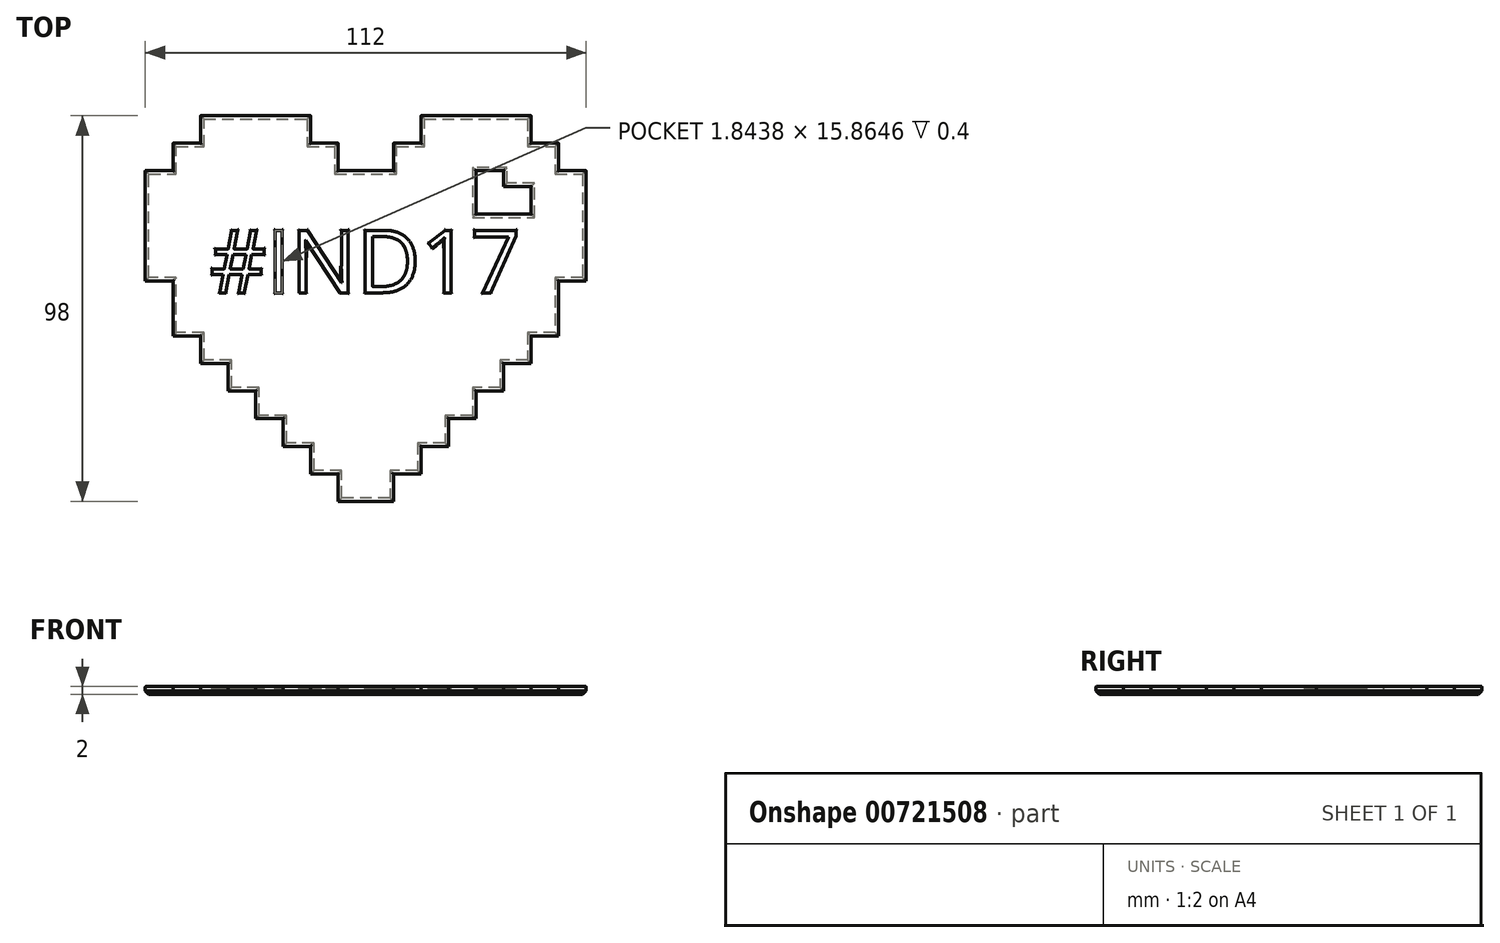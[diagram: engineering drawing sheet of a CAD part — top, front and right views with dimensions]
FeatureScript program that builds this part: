
annotation { "Feature Type Name" : "Feature", "Feature Type Description" : "" }
export const myFeature = defineFeature(function(context is Context, id is Id, definition is map)
    precondition{}
    {
        {
            assignVariable(context, id + "F0", {"variableType" : VariableType.NUMBER, "name" : "scale", "numberValue" : 7});
        }
        {
            var Q0;
            Q0=qCreatedBy(makeId("Top.planeOp"),FACE);
            var sketch = newSketch(context, id + "F1", { "sketchPlane" : qUnion([Q0])});
            skLineSegment(sketch, "E0", {"start": v(25.3, 16.05) * mm, "end": v(25.3, 20.05) * mm});
            skLineSegment(sketch, "E1", {"start": v(18.3, 20.05) * mm, "end": v(18.3, 9.05) * mm});
            skLineSegment(sketch, "E2", {"start": v(18.3, 9.05) * mm, "end": v(32.3, 9.05) * mm});
            skLineSegment(sketch, "E3", {"start": v(32.3, 9.05) * mm, "end": v(32.3, 16.05) * mm});
            skLineSegment(sketch, "E4", {"start": v(32.3, 16.05) * mm, "end": v(25.3, 16.05) * mm});
            skLineSegment(sketch, "E5", {"start": v(39.3, 20.05) * mm, "end": v(39.3, 27.05) * mm});
            skLineSegment(sketch, "E6", {"start": v(39.3, 27.05) * mm, "end": v(32.3, 27.05) * mm});
            skLineSegment(sketch, "E7", {"start": v(32.3, 27.05) * mm, "end": v(32.3, 34.05) * mm});
            skLineSegment(sketch, "E8", {"start": v(32.3, 34.05) * mm, "end": v(4.3, 34.05) * mm});
            skLineSegment(sketch, "E9", {"start": v(4.3, 34.05) * mm, "end": v(4.3, 27.05) * mm});
            skLineSegment(sketch, "E10", {"start": v(4.3, 27.05) * mm, "end": v(-2.7, 27.05) * mm});
            skLineSegment(sketch, "E11", {"start": v(-2.7, 27.05) * mm, "end": v(-2.7, 20.05) * mm});
            skLineSegment(sketch, "E12", {"start": v(-2.7, 20.05) * mm, "end": v(-16.7, 20.05) * mm});
            skLineSegment(sketch, "E13", {"start": v(-16.7, 20.05) * mm, "end": v(-16.7, 27.05) * mm});
            skLineSegment(sketch, "E14", {"start": v(-16.7, 27.05) * mm, "end": v(-23.7, 27.05) * mm});
            skLineSegment(sketch, "E15", {"start": v(-23.7, 27.05) * mm, "end": v(-23.7, 34.05) * mm});
            skLineSegment(sketch, "E16", {"start": v(-23.7, 34.05) * mm, "end": v(-51.7, 34.05) * mm});
            skLineSegment(sketch, "E17", {"start": v(-51.7, 34.05) * mm, "end": v(-51.7, 27.05) * mm});
            skLineSegment(sketch, "E18", {"start": v(-51.7, 27.05) * mm, "end": v(-58.7, 27.05) * mm});
            skLineSegment(sketch, "E19", {"start": v(-58.7, 27.05) * mm, "end": v(-58.7, 20.05) * mm});
            skLineSegment(sketch, "E20", {"start": v(-58.7, 20.05) * mm, "end": v(-65.7, 20.05) * mm});
            skLineSegment(sketch, "E21", {"start": v(-65.7, 20.05) * mm, "end": v(-65.7, -7.95) * mm});
            skLineSegment(sketch, "E22", {"start": v(-65.7, -7.95) * mm, "end": v(-58.7, -7.95) * mm});
            skLineSegment(sketch, "E23", {"start": v(-58.7, -7.95) * mm, "end": v(-58.7, -21.95) * mm});
            skLineSegment(sketch, "E24", {"start": v(-58.7, -21.95) * mm, "end": v(-51.7, -21.95) * mm});
            skLineSegment(sketch, "E25", {"start": v(-51.7, -21.95) * mm, "end": v(-51.7, -28.95) * mm});
            skLineSegment(sketch, "E26", {"start": v(-51.7, -28.95) * mm, "end": v(-44.7, -28.95) * mm});
            skLineSegment(sketch, "E27", {"start": v(-44.7, -28.95) * mm, "end": v(-44.7, -35.95) * mm});
            skLineSegment(sketch, "E28", {"start": v(-44.7, -35.95) * mm, "end": v(-37.7, -35.95) * mm});
            skLineSegment(sketch, "E29", {"start": v(-37.7, -35.95) * mm, "end": v(-37.7, -42.95) * mm});
            skLineSegment(sketch, "E30", {"start": v(-37.7, -42.95) * mm, "end": v(-30.7, -42.95) * mm});
            skLineSegment(sketch, "E31", {"start": v(-30.7, -42.95) * mm, "end": v(-30.7, -49.95) * mm});
            skLineSegment(sketch, "E32", {"start": v(-30.7, -49.95) * mm, "end": v(-23.7, -49.95) * mm});
            skLineSegment(sketch, "E33", {"start": v(-23.7, -49.95) * mm, "end": v(-23.7, -56.95) * mm});
            skLineSegment(sketch, "E34", {"start": v(-23.7, -56.95) * mm, "end": v(-16.7, -56.95) * mm});
            skLineSegment(sketch, "E35", {"start": v(-16.7, -56.95) * mm, "end": v(-16.7, -63.95) * mm});
            skLineSegment(sketch, "E36", {"start": v(-16.7, -63.95) * mm, "end": v(-2.7, -63.95) * mm});
            skLineSegment(sketch, "E37", {"start": v(-2.7, -63.95) * mm, "end": v(-2.7, -56.95) * mm});
            skLineSegment(sketch, "E38", {"start": v(-2.7, -56.95) * mm, "end": v(4.3, -56.95) * mm});
            skLineSegment(sketch, "E39", {"start": v(4.3, -56.95) * mm, "end": v(4.3, -49.95) * mm});
            skLineSegment(sketch, "E40", {"start": v(4.3, -49.95) * mm, "end": v(11.3, -49.95) * mm});
            skLineSegment(sketch, "E41", {"start": v(11.3, -49.95) * mm, "end": v(11.3, -42.95) * mm});
            skLineSegment(sketch, "E42", {"start": v(11.3, -42.95) * mm, "end": v(18.3, -42.95) * mm});
            skLineSegment(sketch, "E43", {"start": v(18.3, -42.95) * mm, "end": v(18.3, -35.95) * mm});
            skLineSegment(sketch, "E44", {"start": v(18.3, -35.95) * mm, "end": v(25.3, -35.95) * mm});
            skLineSegment(sketch, "E45", {"start": v(25.3, -35.95) * mm, "end": v(25.3, -28.95) * mm});
            skLineSegment(sketch, "E46", {"start": v(25.3, -28.95) * mm, "end": v(32.3, -28.95) * mm});
            skLineSegment(sketch, "E47", {"start": v(32.3, -28.95) * mm, "end": v(32.3, -21.95) * mm});
            skLineSegment(sketch, "E48", {"start": v(32.3, -21.95) * mm, "end": v(39.3, -21.95) * mm});
            skLineSegment(sketch, "E49", {"start": v(39.3, -21.95) * mm, "end": v(39.3, -7.95) * mm});
            skLineSegment(sketch, "E50", {"start": v(39.3, -7.95) * mm, "end": v(46.3, -7.95) * mm});
            skLineSegment(sketch, "E51", {"start": v(46.3, -7.95) * mm, "end": v(46.3, 20.05) * mm});
            skLineSegment(sketch, "E52", {"start": v(46.3, 20.05) * mm, "end": v(39.3, 20.05) * mm});
            skLineSegment(sketch, "E53", {"start": v(18.3, 20.05) * mm, "end": v(25.3, 20.05) * mm});
            skSolve(sketch);
        }
        {
            var Q0;
            Q0=makeQuery(id+"F1.imprint","IMPRINT",FACE,{"disambiguationData":[TD([[makeQuery(id+"F1.imprint","IMPRINT",EDGE,{"derivedFrom":sQuery(id+"F1.wireOp",EDGE,"E0")}),-1.0]])]});
            extrude(context, id + "F2", {"entities" : qUnion([Q0]), "depth" : 2 * mm, "offsetDistance" : 25 * mm});
        }
        {
            var Q0;
            Q0=makeQuery(id+"F2.opExtrude","CAP_FACE",FACE,{"disambiguationData":[OSD([sQuery(id+"F1.wireOp",EDGE,"E0"),sQuery(id+"F1.wireOp",EDGE,"E1"),sQuery(id+"F1.wireOp",EDGE,"E2"),sQuery(id+"F1.wireOp",EDGE,"E3"),sQuery(id+"F1.wireOp",EDGE,"E4"),sQuery(id+"F1.wireOp",EDGE,"E5"),sQuery(id+"F1.wireOp",EDGE,"E6"),sQuery(id+"F1.wireOp",EDGE,"E7"),sQuery(id+"F1.wireOp",EDGE,"E8"),sQuery(id+"F1.wireOp",EDGE,"E9"),sQuery(id+"F1.wireOp",EDGE,"E10"),sQuery(id+"F1.wireOp",EDGE,"E11"),sQuery(id+"F1.wireOp",EDGE,"E12"),sQuery(id+"F1.wireOp",EDGE,"E13"),sQuery(id+"F1.wireOp",EDGE,"E14"),sQuery(id+"F1.wireOp",EDGE,"E15"),sQuery(id+"F1.wireOp",EDGE,"E16"),sQuery(id+"F1.wireOp",EDGE,"E17"),sQuery(id+"F1.wireOp",EDGE,"E18"),sQuery(id+"F1.wireOp",EDGE,"E19"),sQuery(id+"F1.wireOp",EDGE,"E20"),sQuery(id+"F1.wireOp",EDGE,"E21"),sQuery(id+"F1.wireOp",EDGE,"E22"),sQuery(id+"F1.wireOp",EDGE,"E23"),sQuery(id+"F1.wireOp",EDGE,"E24"),sQuery(id+"F1.wireOp",EDGE,"E25"),sQuery(id+"F1.wireOp",EDGE,"E26"),sQuery(id+"F1.wireOp",EDGE,"E27"),sQuery(id+"F1.wireOp",EDGE,"E28"),sQuery(id+"F1.wireOp",EDGE,"E29"),sQuery(id+"F1.wireOp",EDGE,"E30"),sQuery(id+"F1.wireOp",EDGE,"E31"),sQuery(id+"F1.wireOp",EDGE,"E32"),sQuery(id+"F1.wireOp",EDGE,"E33"),sQuery(id+"F1.wireOp",EDGE,"E34"),sQuery(id+"F1.wireOp",EDGE,"E35"),sQuery(id+"F1.wireOp",EDGE,"E36"),sQuery(id+"F1.wireOp",EDGE,"E37"),sQuery(id+"F1.wireOp",EDGE,"E38"),sQuery(id+"F1.wireOp",EDGE,"E39"),sQuery(id+"F1.wireOp",EDGE,"E40"),sQuery(id+"F1.wireOp",EDGE,"E41"),sQuery(id+"F1.wireOp",EDGE,"E42"),sQuery(id+"F1.wireOp",EDGE,"E43"),sQuery(id+"F1.wireOp",EDGE,"E44"),sQuery(id+"F1.wireOp",EDGE,"E45"),sQuery(id+"F1.wireOp",EDGE,"E46"),sQuery(id+"F1.wireOp",EDGE,"E47"),sQuery(id+"F1.wireOp",EDGE,"E48"),sQuery(id+"F1.wireOp",EDGE,"E49"),sQuery(id+"F1.wireOp",EDGE,"E50"),sQuery(id+"F1.wireOp",EDGE,"E51"),sQuery(id+"F1.wireOp",EDGE,"E52"),sQuery(id+"F1.wireOp",EDGE,"E53")])],"isStart":true});
            chamfer(context, id + "F3", {"entities" : qUnion([Q0]), "width" : (getVariable(context, 'scale') / 8) * mm, "tangentPropagation" : true});
        }
        {
            var Q0;
            Q0=makeQuery(id+"F2.opExtrude","CAP_FACE",FACE,{"disambiguationData":[OSD([sQuery(id+"F1.wireOp",EDGE,"E0"),sQuery(id+"F1.wireOp",EDGE,"E1"),sQuery(id+"F1.wireOp",EDGE,"E2"),sQuery(id+"F1.wireOp",EDGE,"E3"),sQuery(id+"F1.wireOp",EDGE,"E4"),sQuery(id+"F1.wireOp",EDGE,"E5"),sQuery(id+"F1.wireOp",EDGE,"E6"),sQuery(id+"F1.wireOp",EDGE,"E7"),sQuery(id+"F1.wireOp",EDGE,"E8"),sQuery(id+"F1.wireOp",EDGE,"E9"),sQuery(id+"F1.wireOp",EDGE,"E10"),sQuery(id+"F1.wireOp",EDGE,"E11"),sQuery(id+"F1.wireOp",EDGE,"E12"),sQuery(id+"F1.wireOp",EDGE,"E13"),sQuery(id+"F1.wireOp",EDGE,"E14"),sQuery(id+"F1.wireOp",EDGE,"E15"),sQuery(id+"F1.wireOp",EDGE,"E16"),sQuery(id+"F1.wireOp",EDGE,"E17"),sQuery(id+"F1.wireOp",EDGE,"E18"),sQuery(id+"F1.wireOp",EDGE,"E19"),sQuery(id+"F1.wireOp",EDGE,"E20"),sQuery(id+"F1.wireOp",EDGE,"E21"),sQuery(id+"F1.wireOp",EDGE,"E22"),sQuery(id+"F1.wireOp",EDGE,"E23"),sQuery(id+"F1.wireOp",EDGE,"E24"),sQuery(id+"F1.wireOp",EDGE,"E25"),sQuery(id+"F1.wireOp",EDGE,"E26"),sQuery(id+"F1.wireOp",EDGE,"E27"),sQuery(id+"F1.wireOp",EDGE,"E28"),sQuery(id+"F1.wireOp",EDGE,"E29"),sQuery(id+"F1.wireOp",EDGE,"E30"),sQuery(id+"F1.wireOp",EDGE,"E31"),sQuery(id+"F1.wireOp",EDGE,"E32"),sQuery(id+"F1.wireOp",EDGE,"E33"),sQuery(id+"F1.wireOp",EDGE,"E34"),sQuery(id+"F1.wireOp",EDGE,"E35"),sQuery(id+"F1.wireOp",EDGE,"E36"),sQuery(id+"F1.wireOp",EDGE,"E37"),sQuery(id+"F1.wireOp",EDGE,"E38"),sQuery(id+"F1.wireOp",EDGE,"E39"),sQuery(id+"F1.wireOp",EDGE,"E40"),sQuery(id+"F1.wireOp",EDGE,"E41"),sQuery(id+"F1.wireOp",EDGE,"E42"),sQuery(id+"F1.wireOp",EDGE,"E43"),sQuery(id+"F1.wireOp",EDGE,"E44"),sQuery(id+"F1.wireOp",EDGE,"E45"),sQuery(id+"F1.wireOp",EDGE,"E46"),sQuery(id+"F1.wireOp",EDGE,"E47"),sQuery(id+"F1.wireOp",EDGE,"E48"),sQuery(id+"F1.wireOp",EDGE,"E49"),sQuery(id+"F1.wireOp",EDGE,"E50"),sQuery(id+"F1.wireOp",EDGE,"E51"),sQuery(id+"F1.wireOp",EDGE,"E52"),sQuery(id+"F1.wireOp",EDGE,"E53")])],"isStart":false});
            var sketch = newSketch(context, id + "F4", { "sketchPlane" : qUnion([Q0])});
            skText(sketch, "E54", { "text": "#IND17", "fontName": "OpenSans-Regular.ttf"});
            skLineSegment(sketch, "E55", {"start": v(-9.7, 20.05) * mm, "end": v(-9.7, -63.95) * mm, "construction": true});
            const initialGuessF4  = {"E54": [-0.04931, -0.01095, 1, 0, 0.016]};
            skSetInitialGuess(sketch, initialGuessF4);
            skSolve(sketch);
        }
        {
            var Q0;
            Q0 = qSketchRegion(id + "F4", true);
            extrude(context, id + "F5", {"entities" : qUnion([Q0]), "operationType" : NewBodyOperationType.REMOVE, "oppositeDirection" : true, "depth" : 0.6 * mm, "offsetDistance" : 25 * mm});
        }
        {
            var Q0;
            {var subQ0=sQuery(id+"F1.wireOp",EDGE,"E53");var subQ1=sQuery(id+"F1.wireOp",EDGE,"E52");var subQ2=sQuery(id+"F1.wireOp",EDGE,"E51");var subQ3=sQuery(id+"F1.wireOp",EDGE,"E50");var subQ4=sQuery(id+"F1.wireOp",EDGE,"E49");var subQ5=sQuery(id+"F1.wireOp",EDGE,"E48");var subQ6=sQuery(id+"F1.wireOp",EDGE,"E47");var subQ7=sQuery(id+"F1.wireOp",EDGE,"E46");var subQ8=sQuery(id+"F1.wireOp",EDGE,"E20");var subQ9=sQuery(id+"F1.wireOp",EDGE,"E19");var subQ10=sQuery(id+"F1.wireOp",EDGE,"E18");var subQ11=sQuery(id+"F1.wireOp",EDGE,"E17");var subQ12=sQuery(id+"F1.wireOp",EDGE,"E16");var subQ13=sQuery(id+"F1.wireOp",EDGE,"E15");var subQ14=sQuery(id+"F1.wireOp",EDGE,"E14");var subQ15=sQuery(id+"F1.wireOp",EDGE,"E13");var subQ16=sQuery(id+"F1.wireOp",EDGE,"E12");var subQ17=sQuery(id+"F1.wireOp",EDGE,"E11");var subQ18=sQuery(id+"F1.wireOp",EDGE,"E10");var subQ19=sQuery(id+"F1.wireOp",EDGE,"E2");var subQ20=sQuery(id+"F1.wireOp",EDGE,"E1");var subQ21=sQuery(id+"F1.wireOp",EDGE,"E3");var subQ22=sQuery(id+"F1.wireOp",EDGE,"E21");var subQ23=sQuery(id+"F1.wireOp",EDGE,"E0");var subQ24=sQuery(id+"F1.wireOp",EDGE,"E45");var subQ25=sQuery(id+"F1.wireOp",EDGE,"E9");var subQ26=sQuery(id+"F1.wireOp",EDGE,"E4");var subQ27=sQuery(id+"F1.wireOp",EDGE,"E5");var subQ28=sQuery(id+"F1.wireOp",EDGE,"E6");var subQ29=sQuery(id+"F1.wireOp",EDGE,"E7");var subQ30=sQuery(id+"F1.wireOp",EDGE,"E8");var subQ31=sQuery(id+"F1.wireOp",EDGE,"E34");var subQ32=sQuery(id+"F1.wireOp",EDGE,"E22");var subQ33=sQuery(id+"F1.wireOp",EDGE,"E23");var subQ34=sQuery(id+"F1.wireOp",EDGE,"E24");var subQ35=sQuery(id+"F1.wireOp",EDGE,"E37");var subQ36=sQuery(id+"F1.wireOp",EDGE,"E25");var subQ37=sQuery(id+"F1.wireOp",EDGE,"E38");var subQ38=sQuery(id+"F1.wireOp",EDGE,"E26");var subQ39=sQuery(id+"F1.wireOp",EDGE,"E39");var subQ40=sQuery(id+"F1.wireOp",EDGE,"E27");var subQ41=sQuery(id+"F1.wireOp",EDGE,"E40");var subQ42=sQuery(id+"F1.wireOp",EDGE,"E28");var subQ43=sQuery(id+"F1.wireOp",EDGE,"E41");var subQ44=sQuery(id+"F1.wireOp",EDGE,"E29");var subQ45=sQuery(id+"F1.wireOp",EDGE,"E42");var subQ46=sQuery(id+"F1.wireOp",EDGE,"E30");var subQ47=sQuery(id+"F1.wireOp",EDGE,"E43");var subQ48=sQuery(id+"F1.wireOp",EDGE,"E31");var subQ49=sQuery(id+"F1.wireOp",EDGE,"E44");var subQ50=sQuery(id+"F1.wireOp",EDGE,"E32");var subQ51=sQuery(id+"F1.wireOp",EDGE,"E33");var subQ52=sQuery(id+"F1.wireOp",EDGE,"E35");var subQ53=sQuery(id+"F1.wireOp",EDGE,"E36");Q0=makeQuery(id+"F5.boolean.opBoolean","SPLIT",FACE,{"disambiguationData":[TD([makeQuery(id+"F2.opExtrude","SWEPT_FACE",FACE,{"disambiguationData":[OSD([subQ23])]})])],"derivedFrom":makeQuery(id+"F2.opExtrude","CAP_FACE",FACE,{"disambiguationData":[OSD([subQ23,subQ20,subQ19,subQ21,subQ26,subQ27,subQ28,subQ29,subQ30,subQ25,subQ18,subQ17,subQ16,subQ15,subQ14,subQ13,subQ12,subQ11,subQ10,subQ9,subQ8,subQ22,subQ32,subQ33,subQ34,subQ36,subQ38,subQ40,subQ42,subQ44,subQ46,subQ48,subQ50,subQ51,subQ31,subQ52,subQ53,subQ35,subQ37,subQ39,subQ41,subQ43,subQ45,subQ47,subQ49,subQ24,subQ7,subQ6,subQ5,subQ4,subQ3,subQ2,subQ1,subQ0])],"isStart":false})});}
            var Q1;
            Q1=makeQuery(id+"F5.boolean.opBoolean","SPLIT",FACE,{"disambiguationData":[TD([makeQuery(id+"F5.opExtrude","SWEPT_FACE",FACE,{"disambiguationData":[OSD([sQuery(id+"F4.wireOp",EDGE,"E54.sketch_text.stroke-58")])]})])],"derivedFrom":makeQuery(id+"F2.opExtrude","CAP_FACE",FACE,{"disambiguationData":[OSD([sQuery(id+"F1.wireOp",EDGE,"E0"),sQuery(id+"F1.wireOp",EDGE,"E1"),sQuery(id+"F1.wireOp",EDGE,"E2"),sQuery(id+"F1.wireOp",EDGE,"E3"),sQuery(id+"F1.wireOp",EDGE,"E4"),sQuery(id+"F1.wireOp",EDGE,"E5"),sQuery(id+"F1.wireOp",EDGE,"E6"),sQuery(id+"F1.wireOp",EDGE,"E7"),sQuery(id+"F1.wireOp",EDGE,"E8"),sQuery(id+"F1.wireOp",EDGE,"E9"),sQuery(id+"F1.wireOp",EDGE,"E10"),sQuery(id+"F1.wireOp",EDGE,"E11"),sQuery(id+"F1.wireOp",EDGE,"E12"),sQuery(id+"F1.wireOp",EDGE,"E13"),sQuery(id+"F1.wireOp",EDGE,"E14"),sQuery(id+"F1.wireOp",EDGE,"E15"),sQuery(id+"F1.wireOp",EDGE,"E16"),sQuery(id+"F1.wireOp",EDGE,"E17"),sQuery(id+"F1.wireOp",EDGE,"E18"),sQuery(id+"F1.wireOp",EDGE,"E19"),sQuery(id+"F1.wireOp",EDGE,"E20"),sQuery(id+"F1.wireOp",EDGE,"E21"),sQuery(id+"F1.wireOp",EDGE,"E22"),sQuery(id+"F1.wireOp",EDGE,"E23"),sQuery(id+"F1.wireOp",EDGE,"E24"),sQuery(id+"F1.wireOp",EDGE,"E25"),sQuery(id+"F1.wireOp",EDGE,"E26"),sQuery(id+"F1.wireOp",EDGE,"E27"),sQuery(id+"F1.wireOp",EDGE,"E28"),sQuery(id+"F1.wireOp",EDGE,"E29"),sQuery(id+"F1.wireOp",EDGE,"E30"),sQuery(id+"F1.wireOp",EDGE,"E31"),sQuery(id+"F1.wireOp",EDGE,"E32"),sQuery(id+"F1.wireOp",EDGE,"E33"),sQuery(id+"F1.wireOp",EDGE,"E34"),sQuery(id+"F1.wireOp",EDGE,"E35"),sQuery(id+"F1.wireOp",EDGE,"E36"),sQuery(id+"F1.wireOp",EDGE,"E37"),sQuery(id+"F1.wireOp",EDGE,"E38"),sQuery(id+"F1.wireOp",EDGE,"E39"),sQuery(id+"F1.wireOp",EDGE,"E40"),sQuery(id+"F1.wireOp",EDGE,"E41"),sQuery(id+"F1.wireOp",EDGE,"E42"),sQuery(id+"F1.wireOp",EDGE,"E43"),sQuery(id+"F1.wireOp",EDGE,"E44"),sQuery(id+"F1.wireOp",EDGE,"E45"),sQuery(id+"F1.wireOp",EDGE,"E46"),sQuery(id+"F1.wireOp",EDGE,"E47"),sQuery(id+"F1.wireOp",EDGE,"E48"),sQuery(id+"F1.wireOp",EDGE,"E49"),sQuery(id+"F1.wireOp",EDGE,"E50"),sQuery(id+"F1.wireOp",EDGE,"E51"),sQuery(id+"F1.wireOp",EDGE,"E52"),sQuery(id+"F1.wireOp",EDGE,"E53")])],"isStart":false})});
            var Q2;
            Q2=makeQuery(id+"F5.boolean.opBoolean","SPLIT",FACE,{"disambiguationData":[TD([makeQuery(id+"F5.opExtrude","SWEPT_FACE",FACE,{"disambiguationData":[OSD([sQuery(id+"F4.wireOp",EDGE,"E54.sketch_text.stroke-28")])]})])],"derivedFrom":makeQuery(id+"F2.opExtrude","CAP_FACE",FACE,{"disambiguationData":[OSD([sQuery(id+"F1.wireOp",EDGE,"E0"),sQuery(id+"F1.wireOp",EDGE,"E1"),sQuery(id+"F1.wireOp",EDGE,"E2"),sQuery(id+"F1.wireOp",EDGE,"E3"),sQuery(id+"F1.wireOp",EDGE,"E4"),sQuery(id+"F1.wireOp",EDGE,"E5"),sQuery(id+"F1.wireOp",EDGE,"E6"),sQuery(id+"F1.wireOp",EDGE,"E7"),sQuery(id+"F1.wireOp",EDGE,"E8"),sQuery(id+"F1.wireOp",EDGE,"E9"),sQuery(id+"F1.wireOp",EDGE,"E10"),sQuery(id+"F1.wireOp",EDGE,"E11"),sQuery(id+"F1.wireOp",EDGE,"E12"),sQuery(id+"F1.wireOp",EDGE,"E13"),sQuery(id+"F1.wireOp",EDGE,"E14"),sQuery(id+"F1.wireOp",EDGE,"E15"),sQuery(id+"F1.wireOp",EDGE,"E16"),sQuery(id+"F1.wireOp",EDGE,"E17"),sQuery(id+"F1.wireOp",EDGE,"E18"),sQuery(id+"F1.wireOp",EDGE,"E19"),sQuery(id+"F1.wireOp",EDGE,"E20"),sQuery(id+"F1.wireOp",EDGE,"E21"),sQuery(id+"F1.wireOp",EDGE,"E22"),sQuery(id+"F1.wireOp",EDGE,"E23"),sQuery(id+"F1.wireOp",EDGE,"E24"),sQuery(id+"F1.wireOp",EDGE,"E25"),sQuery(id+"F1.wireOp",EDGE,"E26"),sQuery(id+"F1.wireOp",EDGE,"E27"),sQuery(id+"F1.wireOp",EDGE,"E28"),sQuery(id+"F1.wireOp",EDGE,"E29"),sQuery(id+"F1.wireOp",EDGE,"E30"),sQuery(id+"F1.wireOp",EDGE,"E31"),sQuery(id+"F1.wireOp",EDGE,"E32"),sQuery(id+"F1.wireOp",EDGE,"E33"),sQuery(id+"F1.wireOp",EDGE,"E34"),sQuery(id+"F1.wireOp",EDGE,"E35"),sQuery(id+"F1.wireOp",EDGE,"E36"),sQuery(id+"F1.wireOp",EDGE,"E37"),sQuery(id+"F1.wireOp",EDGE,"E38"),sQuery(id+"F1.wireOp",EDGE,"E39"),sQuery(id+"F1.wireOp",EDGE,"E40"),sQuery(id+"F1.wireOp",EDGE,"E41"),sQuery(id+"F1.wireOp",EDGE,"E42"),sQuery(id+"F1.wireOp",EDGE,"E43"),sQuery(id+"F1.wireOp",EDGE,"E44"),sQuery(id+"F1.wireOp",EDGE,"E45"),sQuery(id+"F1.wireOp",EDGE,"E46"),sQuery(id+"F1.wireOp",EDGE,"E47"),sQuery(id+"F1.wireOp",EDGE,"E48"),sQuery(id+"F1.wireOp",EDGE,"E49"),sQuery(id+"F1.wireOp",EDGE,"E50"),sQuery(id+"F1.wireOp",EDGE,"E51"),sQuery(id+"F1.wireOp",EDGE,"E52"),sQuery(id+"F1.wireOp",EDGE,"E53")])],"isStart":false})});
            fillet(context, id + "F6", {"entities" : qUnion([Q0, Q1, Q2]), "tangentPropagation" : true, "radius" : 0.2 * mm, "defaultsChanged" : false, "vertexSettings" : [], "allowEdgeOverflow" : false});
        }
    });
